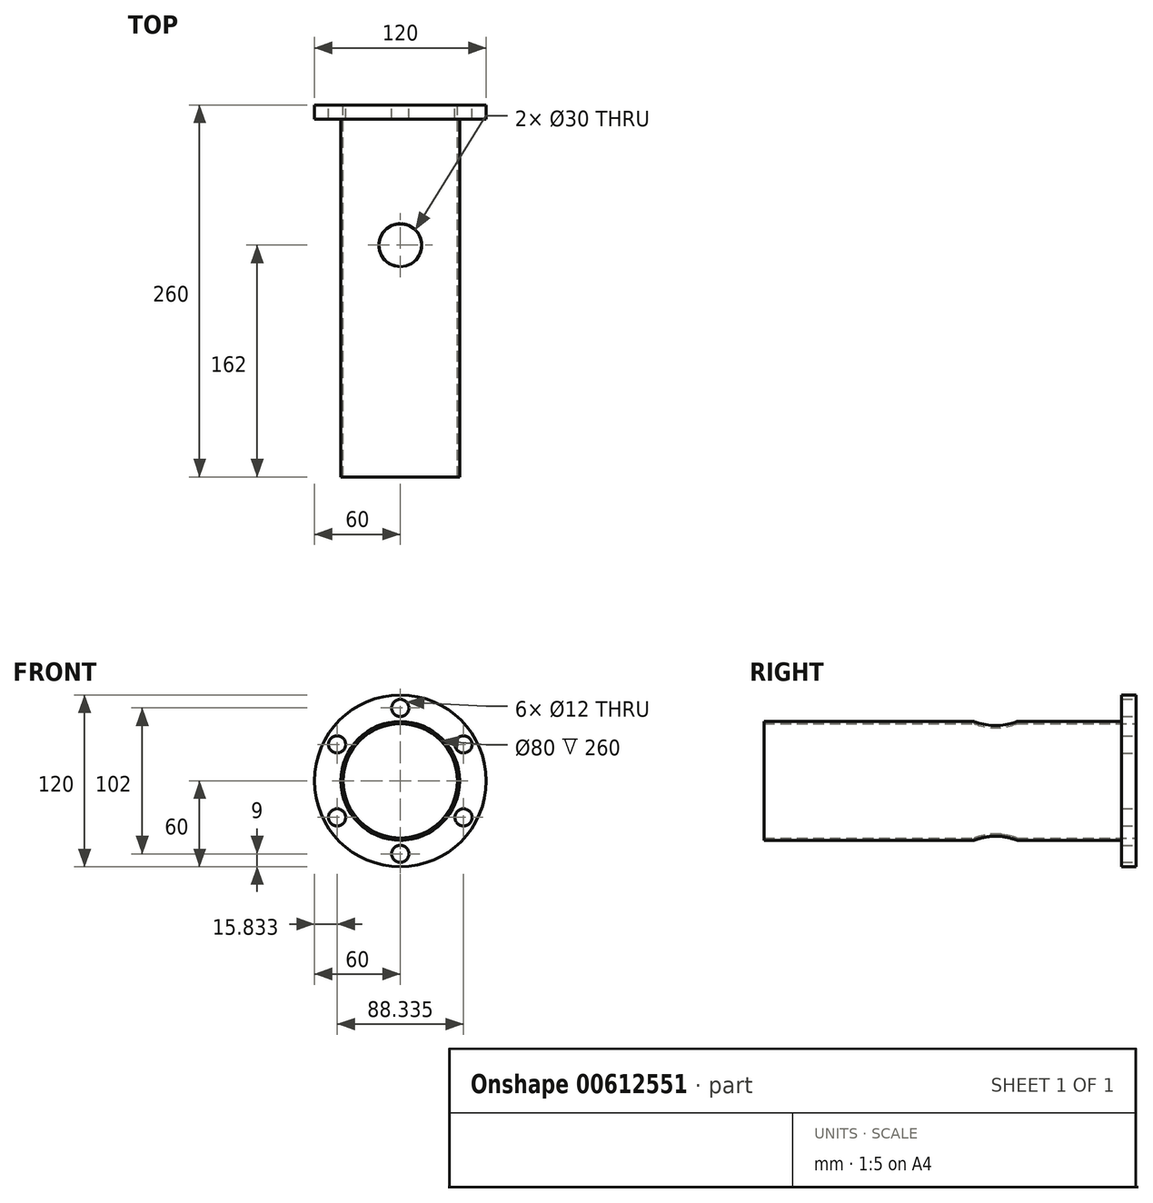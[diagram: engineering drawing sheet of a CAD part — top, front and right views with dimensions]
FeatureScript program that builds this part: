
annotation { "Feature Type Name" : "Feature", "Feature Type Description" : "" }
export const myFeature = defineFeature(function(context is Context, id is Id, definition is map)
    precondition{}
    {
        {
            var Q0;
            Q0=qCreatedBy(makeId("Front.planeOp"),FACE);
            var sketch = newSketch(context, id + "F0", { "sketchPlane" : qUnion([Q0])});
            skCircle(sketch, "E0", {"center": v(0, 0) * mm, "radius": 60 * mm});
            skCircle(sketch, "E1", {"center": v(0, 51) * mm, "radius": 6 * mm});
            skCircle(sketch, "E2.1.0", {"center": v(-44.17, 25.5) * mm, "radius": 6 * mm});
            skCircle(sketch, "E2.2.0", {"center": v(-44.17, -25.5) * mm, "radius": 6 * mm});
            skCircle(sketch, "E2.3.0", {"center": v(0, -51) * mm, "radius": 6 * mm});
            skCircle(sketch, "E2.4.0", {"center": v(44.17, -25.5) * mm, "radius": 6 * mm});
            skCircle(sketch, "E2.5.0", {"center": v(44.17, 25.5) * mm, "radius": 6 * mm});
            skCircle(sketch, "E3", {"center": v(0, 0) * mm, "radius": 40 * mm});
            skSolve(sketch);
        }
        {
            var Q0;
            Q0=makeQuery(id+"F0.imprint","IMPRINT",FACE,{"disambiguationData":[TD([[makeQuery(id+"F0.imprint","IMPRINT",EDGE,{"derivedFrom":sQuery(id+"F0.wireOp",EDGE,"E0")}),1.0]])]});
            extrude(context, id + "F1", {"entities" : qUnion([Q0]), "depth" : 10 * mm, "offsetDistance" : 25 * mm});
        }
        {
            var Q0;
            Q0=makeQuery(id+"F1.opExtrude","CAP_FACE",FACE,{"disambiguationData":[OSD([sQuery(id+"F0.wireOp",EDGE,"E0"),sQuery(id+"F0.wireOp",EDGE,"E1"),sQuery(id+"F0.wireOp",EDGE,"E2.1.0"),sQuery(id+"F0.wireOp",EDGE,"E2.2.0"),sQuery(id+"F0.wireOp",EDGE,"E2.3.0"),sQuery(id+"F0.wireOp",EDGE,"E2.4.0"),sQuery(id+"F0.wireOp",EDGE,"E2.5.0"),sQuery(id+"F0.wireOp",EDGE,"E3")])],"isStart":false});
            var sketch = newSketch(context, id + "F2", { "sketchPlane" : qUnion([Q0])});
            skCircle(sketch, "E4", {"center": v(0, 0) * mm, "radius": 40 * mm});
            skCircle(sketch, "E5", {"center": v(0, 0) * mm, "radius": 41.5 * mm});
            skSolve(sketch);
        }
        {
            var Q0;
            Q0=makeQuery(id+"F2.imprint","IMPRINT",FACE,{"disambiguationData":[TD([[makeQuery(id+"F2.imprint","IMPRINT",EDGE,{"derivedFrom":sQuery(id+"F2.wireOp",EDGE,"E4")}),-1.0]])]});
            extrude(context, id + "F3", {"entities" : qUnion([Q0]), "operationType" : NewBodyOperationType.ADD, "depth" : 250 * mm, "offsetDistance" : 25 * mm});
        }
        {
            var Q0;
            Q0=qCreatedBy(makeId("Top.planeOp"),FACE);
            var sketch = newSketch(context, id + "F4", { "sketchPlane" : qUnion([Q0])});
            skCircle(sketch, "E6", {"center": v(0, -98) * mm, "radius": 15 * mm});
            skSolve(sketch);
        }
        {
            var Q0;
            Q0=makeQuery(id+"F4.imprint","IMPRINT",FACE,{"disambiguationData":[TD([[makeQuery(id+"F4.imprint","IMPRINT",EDGE,{"derivedFrom":sQuery(id+"F4.wireOp",EDGE,"E6")}),1.0]])]});
            extrude(context, id + "F5", {"entities" : qUnion([Q0]), "operationType" : NewBodyOperationType.REMOVE, "oppositeDirection" : true, "depth" : 70.8 * mm, "offsetDistance" : 25 * mm, "hasSecondDirection" : true, "secondDirectionOppositeDirection" : false, "secondDirectionDepth" : 74.6 * mm});
        }
    });
